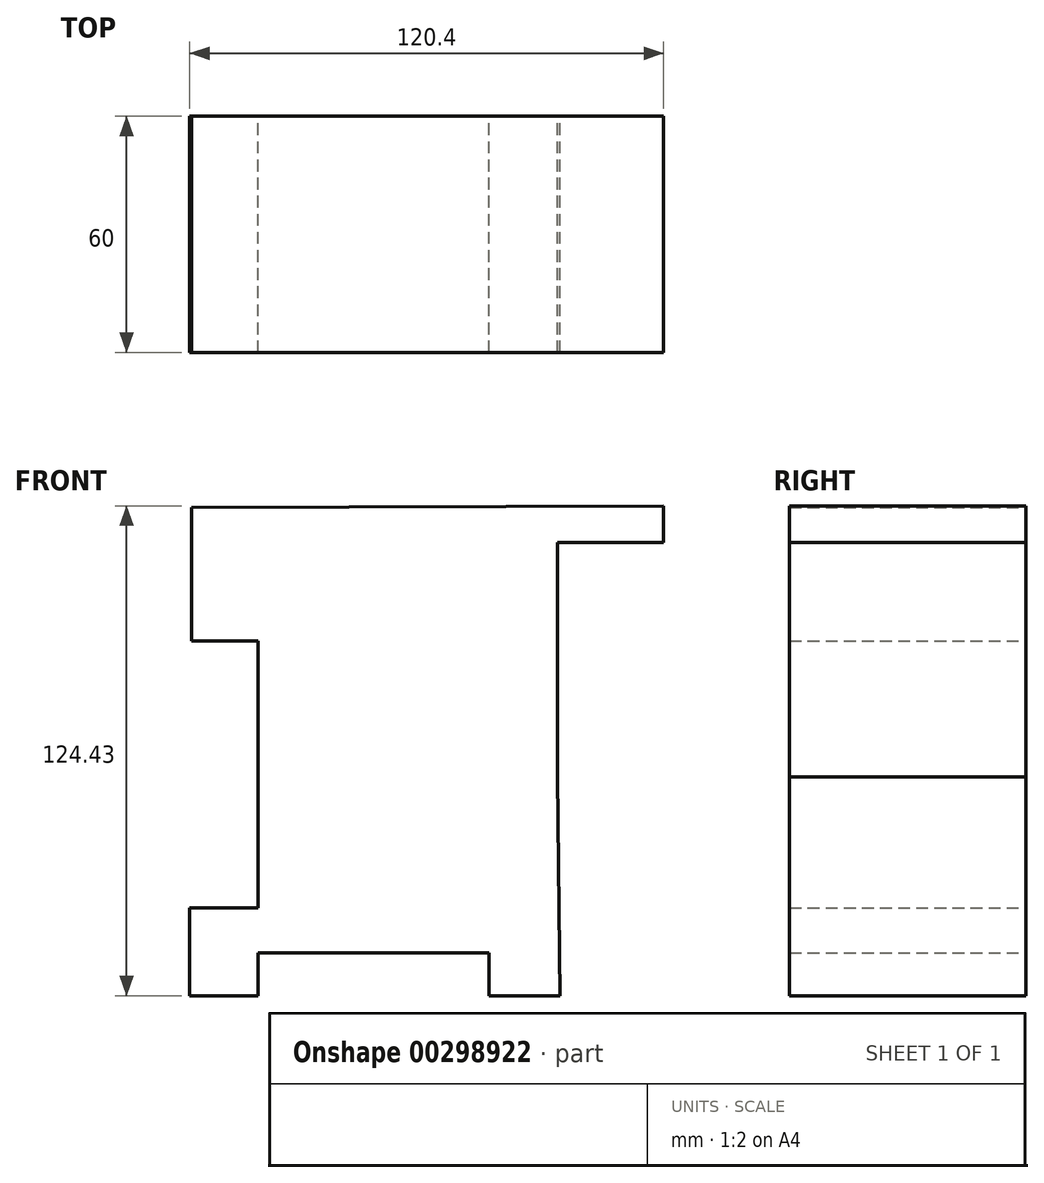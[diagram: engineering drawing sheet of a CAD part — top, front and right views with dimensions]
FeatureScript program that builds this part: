
annotation { "Feature Type Name" : "Feature", "Feature Type Description" : "" }
export const myFeature = defineFeature(function(context is Context, id is Id, definition is map)
    precondition{}
    {
        {
            var Q0;
            Q0=qCreatedBy(makeId("Front.planeOp"),FACE);
            var sketch = newSketch(context, id + "F0", { "sketchPlane" : qUnion([Q0])});
            skLineSegment(sketch, "E0", {"start": v(0, 0) * mm, "end": v(38.07, 0) * mm});
            skLineSegment(sketch, "E1", {"start": v(0, 0) * mm, "end": v(-38.07, 0) * mm});
            skLineSegment(sketch, "E2", {"start": v(-38.07, 0) * mm, "end": v(-38.07, -33.27) * mm});
            skLineSegment(sketch, "E3", {"start": v(-38.07, -33.27) * mm, "end": v(-55.4, -33.27) * mm});
            skLineSegment(sketch, "E4", {"start": v(-55.4, -33.27) * mm, "end": v(-55.4, -55.56) * mm});
            skLineSegment(sketch, "E5", {"start": v(-55.4, -55.56) * mm, "end": v(-38.07, -55.56) * mm});
            skLineSegment(sketch, "E6", {"start": v(-38.07, -55.56) * mm, "end": v(-38.07, -44.64) * mm});
            skLineSegment(sketch, "E7", {"start": v(-38.07, -44.64) * mm, "end": v(20.63, -44.64) * mm});
            skLineSegment(sketch, "E8", {"start": v(20.63, -44.64) * mm, "end": v(20.63, -55.56) * mm});
            skLineSegment(sketch, "E9", {"start": v(20.63, -55.56) * mm, "end": v(38.7, -55.56) * mm});
            skLineSegment(sketch, "E10", {"start": v(38.07, 0) * mm, "end": v(38.7, -55.56) * mm});
            skLineSegment(sketch, "E11", {"start": v(-38.07, 0) * mm, "end": v(-38.07, 34.56) * mm});
            skLineSegment(sketch, "E12", {"start": v(-38.07, 34.56) * mm, "end": v(-54.86, 34.56) * mm});
            skLineSegment(sketch, "E13", {"start": v(-54.86, 34.56) * mm, "end": v(-54.86, 68.53) * mm});
            skLineSegment(sketch, "E14", {"start": v(38.07, 0) * mm, "end": v(38.07, 59.58) * mm});
            skLineSegment(sketch, "E15", {"start": v(38.07, 59.58) * mm, "end": v(65, 59.58) * mm});
            skLineSegment(sketch, "E16", {"start": v(65, 59.58) * mm, "end": v(65, 68.87) * mm});
            skLineSegment(sketch, "E17", {"start": v(65, 68.87) * mm, "end": v(-54.86, 68.53) * mm});
            skSolve(sketch);
        }
        {
            var Q0;
            Q0 = qSketchRegion(id + "F0", true);
            extrude(context, id + "F1", {"entities" : qUnion([Q0]), "depth" : 60 * mm});
        }
    });
